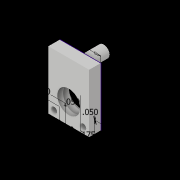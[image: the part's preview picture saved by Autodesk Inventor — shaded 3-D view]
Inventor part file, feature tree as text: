
AUTODESK INVENTOR PART (.ipt)
format: ipt  version: 2017 (Build 210142000, 142)  size: 105,984 bytes
history: native  units: in
note: dims shown in document units (in); Inventor stores cm internally (conversion verified against a paired STEP export)
features: extrude x3, sketch x2, hole x1
ambient origin geometry x8: Origin, YZ Plane, XZ Plane, XY Plane, X Axis, Y Axis, Z Axis, Center Point
bodies: Solid1 (feature_tree)
feature tree (6):
  sketch  "Sketch1"  dims[d0=0.35in d1=0.5in]
  extrude  "Extrusion1"  Depth=0.5in
  extrude  "Extrusion2"  Depth=0.1in
  hole  "Hole1"  [1 undecoded]
  extrude  "Extrusion3"  Depth=0.2in
  sketch  "Sketch2"  dims[d3=0.1in d4=0.0in d5=0.1in d6=0.1in d7=0.175in d8=0.3in d9=0.0in d11=0.196in d12=0.5in d13=0.375in d14=0.25in d15=0.5635in d16=0.75in d17=0.8108in d18=0.05in d19=0.05in d20=0.05in d21=0.05in d22=0.05in d23=0.05in d24=0.2in d25=0.0in d26=0.175in]
note: 1 required parameter value undecoded (feature->parameter linkage not recoverable at this tier; creation-order binding heuristic only, values carry confidence <= 0.55)
